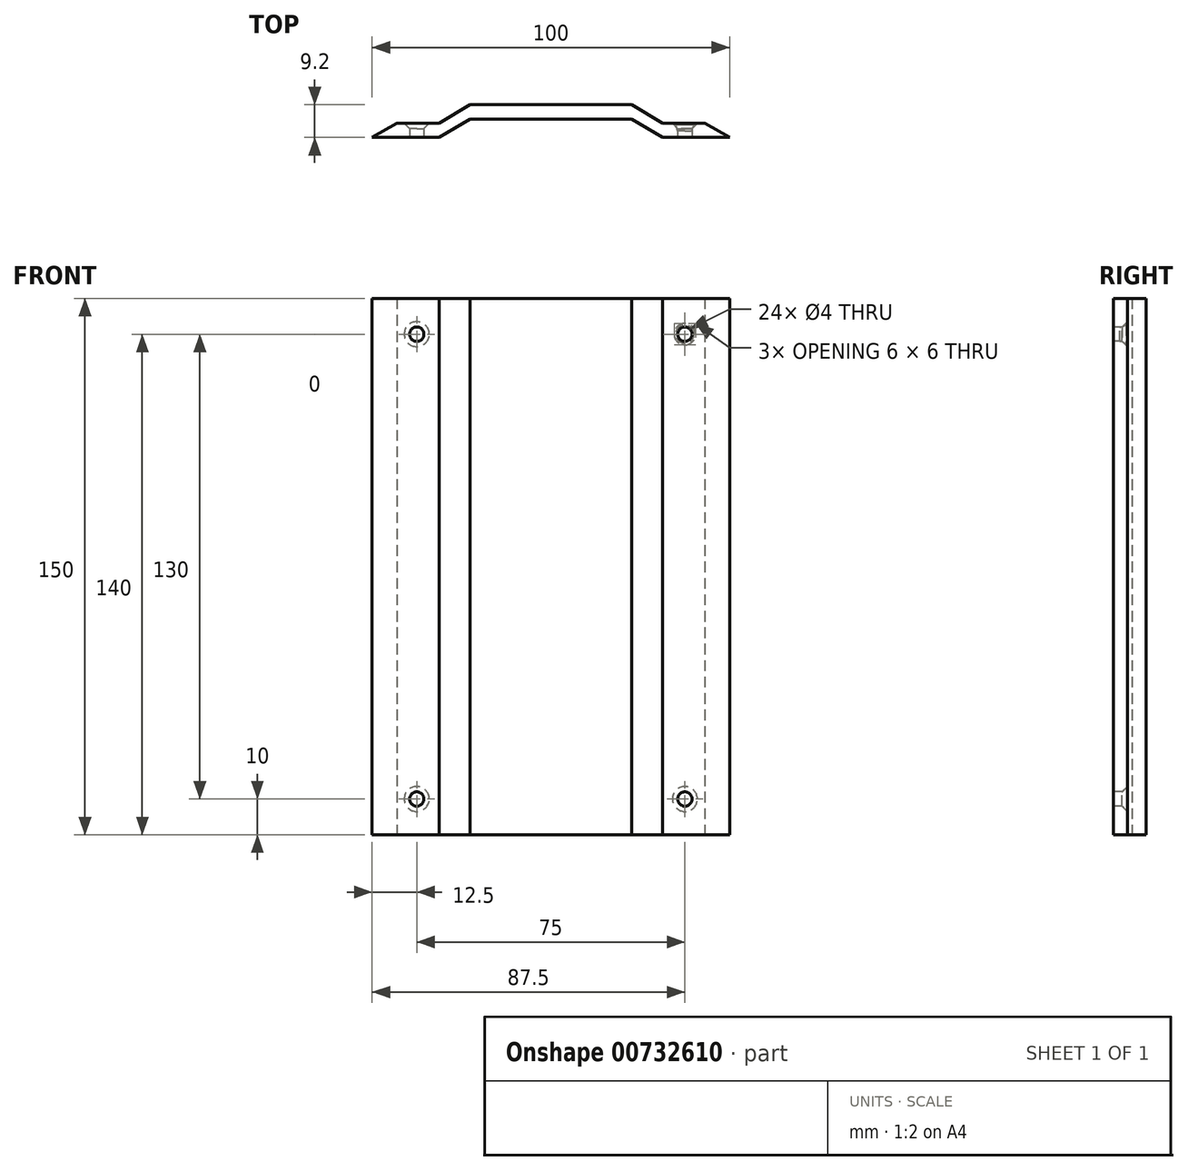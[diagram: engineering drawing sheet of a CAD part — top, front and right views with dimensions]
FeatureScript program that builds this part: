
annotation { "Feature Type Name" : "Feature", "Feature Type Description" : "" }
export const myFeature = defineFeature(function(context is Context, id is Id, definition is map)
    precondition{}
    {
        {
            var Q0;
            Q0=qCreatedBy(makeId("Top.planeOp"),FACE);
            var sketch = newSketch(context, id + "F0", { "sketchPlane" : qUnion([Q0])});
            skLineSegment(sketch, "E0.bottom", {"start": v(0, 0) * mm, "end": v(22.56, 0) * mm});
            skLineSegment(sketch, "E0.top", {"start": v(0, -4) * mm, "end": v(22.56, -4) * mm});
            skLineSegment(sketch, "E0.left", {"start": v(0, 0) * mm, "end": v(0, -4) * mm});
            skLineSegment(sketch, "E0.right", {"start": v(22.56, 0) * mm, "end": v(22.56, -4) * mm});
            skLineSegment(sketch, "E1", {"start": v(0, -4) * mm, "end": v(-8.72, -9.2) * mm});
            skLineSegment(sketch, "E2", {"start": v(-8.72, -9.2) * mm, "end": v(-27.44, -9.2) * mm});
            skLineSegment(sketch, "E3", {"start": v(-27.44, -9.2) * mm, "end": v(-20.51, -5.2) * mm});
            skLineSegment(sketch, "E4", {"start": v(-20.51, -5.2) * mm, "end": v(-8.72, -5.2) * mm});
            skLineSegment(sketch, "E5", {"start": v(-8.72, -5.2) * mm, "end": v(0, 0) * mm});
            skLineSegment(sketch, "E6.MirrorCS", {"start": v(45.12, 0) * mm, "end": v(22.56, 0) * mm});
            skLineSegment(sketch, "E7.MirrorCS", {"start": v(45.12, -4) * mm, "end": v(22.56, -4) * mm});
            skLineSegment(sketch, "E8.MirrorCS", {"start": v(45.12, 0) * mm, "end": v(45.12, -4) * mm});
            skLineSegment(sketch, "E9.MirrorCS", {"start": v(45.12, -4) * mm, "end": v(53.84, -9.2) * mm});
            skLineSegment(sketch, "E10.MirrorCS", {"start": v(53.84, -9.2) * mm, "end": v(72.56, -9.2) * mm});
            skLineSegment(sketch, "E11.MirrorCS", {"start": v(72.56, -9.2) * mm, "end": v(65.63, -5.2) * mm});
            skLineSegment(sketch, "E12.MirrorCS", {"start": v(65.63, -5.2) * mm, "end": v(53.84, -5.2) * mm});
            skLineSegment(sketch, "E13.MirrorCS", {"start": v(53.84, -5.2) * mm, "end": v(45.12, 0) * mm});
            skSolve(sketch);
        }
        {
            var Q0;
            Q0=makeQuery(id+"F0.imprint","IMPRINT",FACE,{"disambiguationData":[TD([[makeQuery(id+"F0.imprint","IMPRINT",EDGE,{"derivedFrom":sQuery(id+"F0.wireOp",EDGE,"E0.left")}),-1.0]])]});
            var Q1;
            Q1=makeQuery(id+"F0.imprint","IMPRINT",FACE,{"disambiguationData":[TD([[makeQuery(id+"F0.imprint","IMPRINT",EDGE,{"derivedFrom":sQuery(id+"F0.wireOp",EDGE,"E0.bottom")}),-1.0]])]});
            var Q2;
            Q2=makeQuery(id+"F0.imprint","IMPRINT",FACE,{"disambiguationData":[TD([[makeQuery(id+"F0.imprint","IMPRINT",EDGE,{"derivedFrom":sQuery(id+"F0.wireOp",EDGE,"E0.right")}),1.0]])]});
            var Q3;
            Q3=makeQuery(id+"F0.imprint","IMPRINT",FACE,{"disambiguationData":[TD([[makeQuery(id+"F0.imprint","IMPRINT",EDGE,{"derivedFrom":sQuery(id+"F0.wireOp",EDGE,"E8.MirrorCS")}),1.0]])]});
            extrude(context, id + "F1", {"entities" : qUnion([Q0, Q1, Q2, Q3]), "depth" : 150 * mm, "offsetDistance" : 25 * mm});
        }
        {
            var Q0;
            Q0=makeQuery(id+"F1.opExtrude","SWEPT_FACE",FACE,{"disambiguationData":[OSD([sQuery(id+"F0.wireOp",EDGE,"E2")])]});
            var sketch = newSketch(context, id + "F2", { "sketchPlane" : qUnion([Q0])});
            skCircle(sketch, "E14", {"center": v(-14.94, 140) * mm, "radius": 2 * mm});
            skLineSegment(sketch, "E15", {"start": v(22.56, 149.85) * mm, "end": v(22.56, 0) * mm, "construction": true});
            skLineSegment(sketch, "E16", {"start": v(-27.44, 75) * mm, "end": v(72.57, 75) * mm, "construction": true});
            skCircle(sketch, "E17.MirrorC", {"center": v(60.06, 140) * mm, "radius": 2 * mm});
            skCircle(sketch, "E18.MirrorC", {"center": v(-14.94, 10) * mm, "radius": 2 * mm});
            skCircle(sketch, "E19.MirrorC", {"center": v(60.06, 10) * mm, "radius": 2 * mm});
            skSolve(sketch);
        }
        {
            var Q0;
            Q0 = qSketchRegion(id + "F2", true);
            extrude(context, id + "F3", {"entities" : qUnion([Q0]), "operationType" : NewBodyOperationType.REMOVE, "endBound" : BoundingType.THROUGH_ALL, "oppositeDirection" : true, "depth" : 25 * mm, "offsetDistance" : 25 * mm});
        }
        {
            var Q0;
            Q0=makeQuery(id+"F3.boolean.opBoolean","INTERSECT",EDGE,{"derivedFrom":[makeQuery(id+"F1.opExtrude","SWEPT_FACE",FACE,{"disambiguationData":[OSD([sQuery(id+"F0.wireOp",EDGE,"E12.MirrorCS")])]}),makeQuery(id+"F3.opExtrude","SWEPT_FACE",FACE,{"disambiguationData":[OSD([sQuery(id+"F2.wireOp",EDGE,"E17.MirrorC")])]})]});
            chamfer(context, id + "F4", {"entities" : qUnion([Q0]), "width" : 1 * mm, "tangentPropagation" : true});
        }
        {
            var Q0;
            {var subQ0=makeQuery(id+"F3.opExtrude","SWEPT_FACE",FACE,{"disambiguationData":[OSD([sQuery(id+"F2.wireOp",EDGE,"E17.MirrorC")])]});Q0=makeQuery(id+"F4.opChamfer","BLEND_EDGE",EDGE,{"blendedFrom":[makeQuery(id+"F3.boolean.opBoolean","INTERSECT",EDGE,{"derivedFrom":[makeQuery(id+"F1.opExtrude","SWEPT_FACE",FACE,{"disambiguationData":[OSD([sQuery(id+"F0.wireOp",EDGE,"E12.MirrorCS")])]}),subQ0]}),makeQuery(id+"F3.boolean.opBoolean","COPY",FACE,{"derivedFrom":subQ0})],"blendedInto":[makeQuery(id+"F3.boolean.opBoolean","COPY",FACE,{"derivedFrom":subQ0})]});}
            chamfer(context, id + "F5", {"entities" : qUnion([Q0]), "width" : 2 * mm, "tangentPropagation" : true});
        }
        {
            var Q0;
            Q0=makeQuery(id+"F3.boolean.opBoolean","INTERSECT",EDGE,{"derivedFrom":[makeQuery(id+"F1.opExtrude","SWEPT_FACE",FACE,{"disambiguationData":[OSD([sQuery(id+"F0.wireOp",EDGE,"E12.MirrorCS")])]}),makeQuery(id+"F3.opExtrude","SWEPT_FACE",FACE,{"disambiguationData":[OSD([sQuery(id+"F2.wireOp",EDGE,"E19.MirrorC")])]})]});
            var Q1;
            Q1=makeQuery(id+"F3.boolean.opBoolean","INTERSECT",EDGE,{"derivedFrom":[makeQuery(id+"F1.opExtrude","SWEPT_FACE",FACE,{"disambiguationData":[OSD([sQuery(id+"F0.wireOp",EDGE,"E4")])]}),makeQuery(id+"F3.opExtrude","SWEPT_FACE",FACE,{"disambiguationData":[OSD([sQuery(id+"F2.wireOp",EDGE,"E18.MirrorC")])]})]});
            var Q2;
            Q2=makeQuery(id+"F3.boolean.opBoolean","INTERSECT",EDGE,{"derivedFrom":[makeQuery(id+"F1.opExtrude","SWEPT_FACE",FACE,{"disambiguationData":[OSD([sQuery(id+"F0.wireOp",EDGE,"E4")])]}),makeQuery(id+"F3.opExtrude","SWEPT_FACE",FACE,{"disambiguationData":[OSD([sQuery(id+"F2.wireOp",EDGE,"E14")])]})]});
            var Q3;
            {var subQ0=makeQuery(id+"F3.opExtrude","SWEPT_FACE",FACE,{"disambiguationData":[OSD([sQuery(id+"F2.wireOp",EDGE,"E17.MirrorC")])]});var subQ1=makeQuery(id+"F3.boolean.opBoolean","COPY",FACE,{"derivedFrom":subQ0});Q3=makeQuery(id+"F5.opChamfer","BLEND_EDGE",EDGE,{"blendedFrom":[makeQuery(id+"F4.opChamfer","BLEND_EDGE",EDGE,{"blendedFrom":[makeQuery(id+"F3.boolean.opBoolean","INTERSECT",EDGE,{"derivedFrom":[makeQuery(id+"F1.opExtrude","SWEPT_FACE",FACE,{"disambiguationData":[OSD([sQuery(id+"F0.wireOp",EDGE,"E12.MirrorCS")])]}),subQ0]}),subQ1],"blendedInto":[subQ1]}),subQ1],"blendedInto":[subQ1]});}
            chamfer(context, id + "F6", {"entities" : qUnion([Q0, Q1, Q2, Q3]), "width" : 1.5 * mm, "tangentPropagation" : true});
        }
    });
